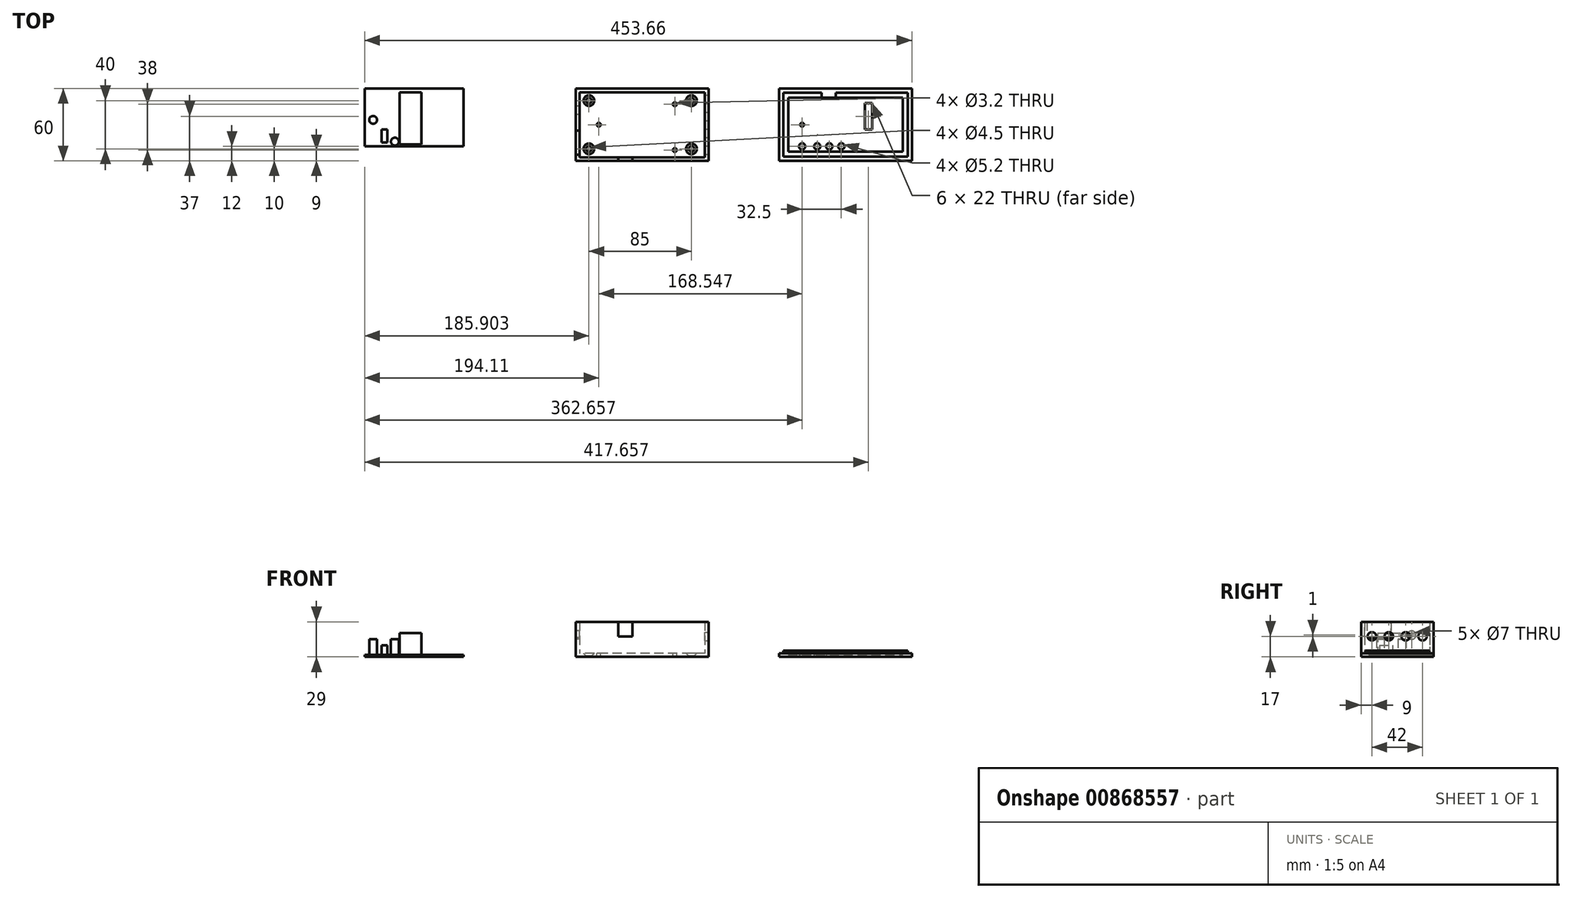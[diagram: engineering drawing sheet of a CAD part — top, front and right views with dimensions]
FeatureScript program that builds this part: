
annotation { "Feature Type Name" : "Feature", "Feature Type Description" : "" }
export const myFeature = defineFeature(function(context is Context, id is Id, definition is map)
    precondition{}
    {
        {
            var Q0;
            Q0=qCreatedBy(makeId("Top.planeOp"),FACE);
            var sketch = newSketch(context, id + "F0", { "sketchPlane" : qUnion([Q0])});
            skLineSegment(sketch, "E0.bottom", {"start": v(0, 0) * mm, "end": v(-110, 0) * mm});
            skLineSegment(sketch, "E0.top", {"start": v(0, -60) * mm, "end": v(-110, -60) * mm});
            skLineSegment(sketch, "E0.left", {"start": v(0, 0) * mm, "end": v(0, -60) * mm});
            skLineSegment(sketch, "E0.right", {"start": v(-110, 0) * mm, "end": v(-110, -60) * mm});
            skSolve(sketch);
        }
        {
            var Q0;
            Q0=makeQuery(id+"F0.imprint","IMPRINT",FACE,{"disambiguationData":[TD([[makeQuery(id+"F0.imprint","IMPRINT",EDGE,{"derivedFrom":sQuery(id+"F0.wireOp",EDGE,"E0.bottom")}),1.0]])]});
            extrude(context, id + "F1", {"entities" : qUnion([Q0]), "depth" : 3 * mm, "offsetDistance" : 25 * mm});
        }
        {
            var Q0;
            Q0=makeQuery(id+"F1.opExtrude","CAP_FACE",FACE,{"disambiguationData":[OSD([sQuery(id+"F0.wireOp",EDGE,"E0.bottom"),sQuery(id+"F0.wireOp",EDGE,"E0.top"),sQuery(id+"F0.wireOp",EDGE,"E0.left"),sQuery(id+"F0.wireOp",EDGE,"E0.right")])],"isStart":false});
            var sketch = newSketch(context, id + "F2", { "sketchPlane" : qUnion([Q0])});
            skLineSegment(sketch, "E1.0", {"start": v(-107, -3) * mm, "end": v(-107, -57) * mm});
            skLineSegment(sketch, "E1.1", {"start": v(-3, -3) * mm, "end": v(-107, -3) * mm});
            skLineSegment(sketch, "E1.2", {"start": v(-3, -3) * mm, "end": v(-3, -57) * mm});
            skLineSegment(sketch, "E1.3", {"start": v(-3, -57) * mm, "end": v(-107, -57) * mm});
            skPoint(sketch, "E2", {"position": v(-3, -30) * mm});
            skLineSegment(sketch, "E3", {"start": v(-3, -30) * mm, "end": v(-107, -30) * mm, "construction": true});
            skPoint(sketch, "E4", {"position": v(-52, -30) * mm});
            skLineSegment(sketch, "E5", {"start": v(-52, -30) * mm, "end": v(-52, -38.53) * mm, "construction": true});
            skPoint(sketch, "E6", {"position": v(-99.2, -50) * mm});
            skPoint(sketch, "E7.MirrorP", {"position": v(-99.2, -10) * mm});
            skLineSegment(sketch, "E8.MirrorCS", {"start": v(-52, -30) * mm, "end": v(-52, -21.47) * mm, "construction": true});
            skPoint(sketch, "E9", {"position": v(-14.2, -50) * mm});
            skPoint(sketch, "E10.MirrorP", {"position": v(-14.2, -10) * mm});
            skSolve(sketch);
        }
        {
            var Q0;
            Q0=makeQuery(id+"F2.imprint","IMPRINT",FACE,{"disambiguationData":[TD([[makeQuery(id+"F2.imprint","IMPRINT",EDGE,{"derivedFrom":sQuery(id+"F2.wireOp",EDGE,"E1.0")}),-1.0]])]});
            extrude(context, id + "F3", {"entities" : qUnion([Q0]), "operationType" : NewBodyOperationType.ADD, "depth" : 24 * mm, "offsetDistance" : 25 * mm});
        }
        {
            var Q0;
            {var subQ0=sQuery(id+"F0.wireOp",EDGE,"E0.right");Q0=makeQuery(id+"F3.boolean.opBoolean","MERGE",FACE,{"derivedFrom":[makeQuery(id+"F1.opExtrude","SWEPT_FACE",FACE,{"disambiguationData":[OSD([subQ0])]}),makeQuery(id+"F3.opExtrude","SWEPT_FACE",FACE,{"disambiguationData":[OSD([subQ0])]})]});}
            var sketch = newSketch(context, id + "F4", { "sketchPlane" : qUnion([Q0])});
            skPoint(sketch, "E11", {"position": v(45, 24) * mm});
            skPoint(sketch, "E12", {"position": v(18, 18) * mm});
            skCircle(sketch, "E13", {"center": v(18, 18) * mm, "radius": 3.5 * mm});
            skPoint(sketch, "E14", {"position": v(45, 16) * mm});
            skLineSegment(sketch, "E15", {"start": v(45, 16) * mm, "end": v(55, 16) * mm});
            skLineSegment(sketch, "E16", {"start": v(45, 16) * mm, "end": v(35, 16) * mm});
            skLineSegment(sketch, "E17", {"start": v(35, 16) * mm, "end": v(35, 27) * mm});
            skLineSegment(sketch, "E18", {"start": v(55, 16) * mm, "end": v(55, 27) * mm});
            skPoint(sketch, "E18.endSnap0", {"position": v(30, 27) * mm});
            skSolve(sketch);
        }
        {
            var Q0;
            Q0=makeQuery(id+"F4.imprint","IMPRINT",FACE,{"disambiguationData":[TD([[makeQuery(id+"F4.imprint","IMPRINT",EDGE,{"derivedFrom":sQuery(id+"F4.wireOp",EDGE,"a7Mlz7Xj-MbBD-aRSO-vmKB-jrrkiIna5h4T")}),1.0]])]});
            var Q1;
            Q1=makeQuery(id+"F4.imprint","IMPRINT",FACE,{"disambiguationData":[TD([[makeQuery(id+"F4.imprint","IMPRINT",EDGE,{"derivedFrom":sQuery(id+"F4.wireOp",EDGE,"E13")}),1.0]])]});
            var Q2;
            Q2=makeQuery(id+"F4.imprint","IMPRINT",FACE,{"disambiguationData":[TD([[makeQuery(id+"F4.imprint","IMPRINT",EDGE,{"derivedFrom":sQuery(id+"F4.wireOp",EDGE,"E15")}),1.0]])]});
            extrude(context, id + "F5", {"entities" : qUnion([Q0, Q1, Q2]), "operationType" : NewBodyOperationType.REMOVE, "oppositeDirection" : true, "depth" : 25 * mm, "offsetDistance" : 25 * mm});
        }
        {
            var Q0;
            Q0=makeQuery(id+"F2.imprint","IMPRINT",FACE,{"disambiguationData":[TD([[makeQuery(id+"F2.imprint","IMPRINT",EDGE,{"derivedFrom":sQuery(id+"F2.wireOp",EDGE,"E1.0")}),1.0]])]});
            var sketch = newSketch(context, id + "F6", { "sketchPlane" : qUnion([Q0])});
            skPoint(sketch, "E19.0", {"position": v(-107, -30) * mm});
            skPoint(sketch, "E20.0", {"position": v(-107, -3) * mm});
            skPoint(sketch, "E21.0", {"position": v(-107, -57) * mm});
            skPoint(sketch, "E22.0", {"position": v(-3, -3) * mm});
            skPoint(sketch, "E23.0", {"position": v(-3, -30) * mm});
            skPoint(sketch, "E24.0", {"position": v(-3, -57) * mm});
            skPoint(sketch, "E25", {"position": v(-91, -30) * mm});
            skCircle(sketch, "E26", {"center": v(-91, -30) * mm, "radius": 1.6 * mm});
            skPoint(sketch, "E27", {"position": v(-28, -30) * mm});
            skLineSegment(sketch, "E28", {"start": v(-28, -30) * mm, "end": v(-28, -51) * mm, "construction": true});
            skCircle(sketch, "E29", {"center": v(-28, -51) * mm, "radius": 1.6 * mm});
            skCircle(sketch, "E30", {"center": v(-28, -13) * mm, "radius": 1.6 * mm});
            skSolve(sketch);
        }
        {
            var Q0;
            Q0=makeQuery(id+"F6.imprint","IMPRINT",FACE,{"disambiguationData":[TD([[makeQuery(id+"F6.imprint","IMPRINT",EDGE,{"derivedFrom":sQuery(id+"F6.wireOp",EDGE,"E29")}),1.0]])]});
            var Q1;
            Q1=makeQuery(id+"F6.imprint","IMPRINT",FACE,{"disambiguationData":[TD([[makeQuery(id+"F6.imprint","IMPRINT",EDGE,{"derivedFrom":sQuery(id+"F6.wireOp",EDGE,"E30")}),1.0]])]});
            var Q2;
            Q2=makeQuery(id+"F6.imprint","IMPRINT",FACE,{"disambiguationData":[TD([[makeQuery(id+"F6.imprint","IMPRINT",EDGE,{"derivedFrom":sQuery(id+"F6.wireOp",EDGE,"E26")}),1.0]])]});
            extrude(context, id + "F7", {"entities" : qUnion([Q0, Q1, Q2]), "operationType" : NewBodyOperationType.REMOVE, "oppositeDirection" : true, "depth" : 25 * mm, "offsetDistance" : 25 * mm});
        }
        {
            var Q0;
            {var subQ0=sQuery(id+"F0.wireOp",EDGE,"E0.top");Q0=makeQuery(id+"F3.boolean.opBoolean","MERGE",FACE,{"derivedFrom":[makeQuery(id+"F1.opExtrude","SWEPT_FACE",FACE,{"disambiguationData":[OSD([subQ0])]}),makeQuery(id+"F3.opExtrude","SWEPT_FACE",FACE,{"disambiguationData":[OSD([subQ0])]})]});}
            var sketch = newSketch(context, id + "F8", { "sketchPlane" : qUnion([Q0])});
            skPoint(sketch, "E31", {"position": v(-75, 27) * mm});
            skPoint(sketch, "E32", {"position": v(-63, 27) * mm});
            skPoint(sketch, "E33", {"position": v(-75, 17) * mm});
            skLineSegment(sketch, "E34", {"start": v(-75, 17) * mm, "end": v(-75, 27) * mm});
            skLineSegment(sketch, "E35", {"start": v(-75, 17) * mm, "end": v(-63, 17) * mm});
            skLineSegment(sketch, "E36", {"start": v(-63, 17) * mm, "end": v(-63, 27) * mm});
            skSolve(sketch);
        }
        {
            var Q0;
            {var subQ0=sQuery(id+"F8.wireOp",EDGE,"E34");Q0=makeQuery(id+"F8.imprint","IMPRINT",FACE,{"disambiguationData":[TD([[makeQuery(id+"F8.imprint","IMPRINT",EDGE,{"derivedFrom":subQ0}),-1.0]])]});}
            extrude(context, id + "F9", {"entities" : qUnion([Q0]), "operationType" : NewBodyOperationType.REMOVE, "oppositeDirection" : true, "depth" : 25 * mm, "offsetDistance" : 25 * mm});
        }
        {
            var Q0;
            {var subQ0=sQuery(id+"F0.wireOp",EDGE,"E0.left");Q0=makeQuery(id+"F3.boolean.opBoolean","MERGE",FACE,{"derivedFrom":[makeQuery(id+"F1.opExtrude","SWEPT_FACE",FACE,{"disambiguationData":[OSD([subQ0])]}),makeQuery(id+"F3.opExtrude","SWEPT_FACE",FACE,{"disambiguationData":[OSD([subQ0])]})]});}
            var sketch = newSketch(context, id + "F10", { "sketchPlane" : qUnion([Q0])});
            skPoint(sketch, "E37", {"position": v(-60, 17) * mm});
            skLineSegment(sketch, "E38", {"start": v(-60, 17) * mm, "end": v(0, 17) * mm, "construction": true});
            skCircle(sketch, "E39", {"center": v(-51, 17) * mm, "radius": 3.5 * mm});
            skCircle(sketch, "E40.1.0.0", {"center": v(-37, 17) * mm, "radius": 3.5 * mm});
            skCircle(sketch, "E40.2.0.0", {"center": v(-23, 17) * mm, "radius": 3.5 * mm});
            skCircle(sketch, "E40.3.0.0", {"center": v(-9, 17) * mm, "radius": 3.5 * mm});
            skLineSegment(sketch, "E40.direction1", {"start": v(-51, 17) * mm, "end": v(-37, 17) * mm, "construction": true});
            skSolve(sketch);
        }
        {
            var Q0;
            Q0=makeQuery(id+"F10.imprint","IMPRINT",FACE,{"disambiguationData":[TD([[makeQuery(id+"F10.imprint","IMPRINT",EDGE,{"derivedFrom":sQuery(id+"F10.wireOp",EDGE,"E39")}),1.0]])]});
            var Q1;
            Q1=makeQuery(id+"F10.imprint","IMPRINT",FACE,{"disambiguationData":[TD([[makeQuery(id+"F10.imprint","IMPRINT",EDGE,{"derivedFrom":sQuery(id+"F10.wireOp",EDGE,"E40.1.0.0")}),1.0]])]});
            var Q2;
            Q2=makeQuery(id+"F10.imprint","IMPRINT",FACE,{"disambiguationData":[TD([[makeQuery(id+"F10.imprint","IMPRINT",EDGE,{"derivedFrom":sQuery(id+"F10.wireOp",EDGE,"E40.2.0.0")}),1.0]])]});
            var Q3;
            Q3=makeQuery(id+"F10.imprint","IMPRINT",FACE,{"disambiguationData":[TD([[makeQuery(id+"F10.imprint","IMPRINT",EDGE,{"derivedFrom":sQuery(id+"F10.wireOp",EDGE,"E40.3.0.0")}),1.0]])]});
            extrude(context, id + "F11", {"entities" : qUnion([Q0, Q1, Q2, Q3]), "operationType" : NewBodyOperationType.REMOVE, "oppositeDirection" : true, "depth" : 25 * mm, "offsetDistance" : 25 * mm});
        }
        {
            var Q0;
            {var subQ0=sQuery(id+"F0.wireOp",EDGE,"E0.top");var subQ1=sQuery(id+"F0.wireOp",EDGE,"E0.bottom");var subQ2=sQuery(id+"F2.wireOp",EDGE,"E1.3");var subQ3=sQuery(id+"F2.wireOp",EDGE,"E1.0");var subQ4=sQuery(id+"F0.wireOp",EDGE,"E0.left");var subQ5=sQuery(id+"F2.wireOp",EDGE,"E1.2");var subQ6=sQuery(id+"F0.wireOp",EDGE,"E0.right");var subQ7=sQuery(id+"F2.wireOp",EDGE,"E1.1");Q0=makeQuery(id+"F9.boolean.opBoolean","SPLIT",FACE,{"disambiguationData":[TD([makeQuery(id+"F1.opExtrude","SWEPT_FACE",FACE,{"disambiguationData":[OSD([subQ1])]})])],"derivedFrom":makeQuery(id+"F3.opExtrude","CAP_FACE",FACE,{"disambiguationData":[OSD([subQ1,subQ0,subQ4,subQ6,subQ3,subQ7,subQ5,subQ2])],"isStart":false})});}
            var Q1;
            {var subQ0=sQuery(id+"F0.wireOp",EDGE,"E0.right");var subQ1=sQuery(id+"F2.wireOp",EDGE,"E1.3");var subQ2=sQuery(id+"F2.wireOp",EDGE,"E1.0");var subQ3=sQuery(id+"F0.wireOp",EDGE,"E0.top");Q1=makeQuery(id+"F9.boolean.opBoolean","SPLIT",FACE,{"disambiguationData":[TD([makeQuery(id+"F5.boolean.opBoolean","COPY",FACE,{"derivedFrom":makeQuery(id+"F5.opExtrude","SWEPT_FACE",FACE,{"disambiguationData":[OSD([sQuery(id+"F4.wireOp",EDGE,"E18")])]})})])],"derivedFrom":makeQuery(id+"F3.opExtrude","CAP_FACE",FACE,{"disambiguationData":[OSD([sQuery(id+"F0.wireOp",EDGE,"E0.bottom"),subQ3,sQuery(id+"F0.wireOp",EDGE,"E0.left"),subQ0,subQ2,sQuery(id+"F2.wireOp",EDGE,"E1.1"),sQuery(id+"F2.wireOp",EDGE,"E1.2"),subQ1])],"isStart":false})});}
            extrude(context, id + "F12", {"entities" : qUnion([Q0, Q1]), "operationType" : NewBodyOperationType.ADD, "depth" : 2 * mm, "offsetDistance" : 25 * mm});
        }
        {
            var Q0;
            Q0=sQuery(id+"F2.wireOp",VERTEX,"E7.MirrorP");
            var Q1;
            Q1=sQuery(id+"F2.wireOp",VERTEX,"E6");
            var Q2;
            Q2=sQuery(id+"F2.wireOp",VERTEX,"E9");
            var Q3;
            Q3=sQuery(id+"F2.wireOp",VERTEX,"E10.MirrorP");
            var Q4;
            Q4=makeQuery(id+"F1.opExtrude","SWEPT_BODY",BODY,{"disambiguationData":[OSD([sQuery(id+"F0.wireOp",EDGE,"E0.bottom"),sQuery(id+"F0.wireOp",EDGE,"E0.top"),sQuery(id+"F0.wireOp",EDGE,"E0.left"),sQuery(id+"F0.wireOp",EDGE,"E0.right")])]});
            hole(context, id + "F13", {"style" : HoleStyle.C_SINK, "endStyle" : HoleEndStyle.THROUGH, "standardTappedOrClearance" : lookupTablePath({ "fit" : "Normal", "standard" : "ISO", "size" : "M4", "type" : "Clearance" }), "standardBlindInLast" : lookupTablePath({ "fit" : "Normal", "standard" : "ISO", "size" : "M4", "type" : "Clearance" }), "holeDiameter" : 4.5 * mm, "cSinkDiameter" : 8.96 * mm, "cSinkAngle" : 90 * degree, "majorDiameter" : 4 * mm, "isTappedThrough" : true, "tappedDepth" : 12 * mm, "tapClearance" : 3, "locations" : qUnion([Q0, Q1, Q2, Q3]), "scope" : qUnion([Q4])});
        }
        {
            var Q0;
            Q0=qCreatedBy(makeId("Top.planeOp"),FACE);
            var sketch = newSketch(context, id + "F14", { "sketchPlane" : qUnion([Q0])});
            skLineSegment(sketch, "E41.bottom", {"start": v(58.55, 0) * mm, "end": v(168.55, 0) * mm});
            skLineSegment(sketch, "E41.top", {"start": v(58.55, -60) * mm, "end": v(168.55, -60) * mm});
            skLineSegment(sketch, "E41.left", {"start": v(58.55, 0) * mm, "end": v(58.55, -60) * mm});
            skLineSegment(sketch, "E41.right", {"start": v(168.55, 0) * mm, "end": v(168.55, -60) * mm});
            skSolve(sketch);
        }
        {
            var Q0;
            Q0=makeQuery(id+"F14.imprint","IMPRINT",FACE,{"disambiguationData":[TD([[makeQuery(id+"F14.imprint","IMPRINT",EDGE,{"derivedFrom":sQuery(id+"F14.wireOp",EDGE,"E41.bottom")}),-1.0]])]});
            extrude(context, id + "F15", {"entities" : qUnion([Q0]), "depth" : 3 * mm, "offsetDistance" : 25 * mm});
        }
        {
            var Q0;
            Q0=makeQuery(id+"F15.opExtrude","CAP_FACE",FACE,{"disambiguationData":[OSD([sQuery(id+"F14.wireOp",EDGE,"E41.bottom"),sQuery(id+"F14.wireOp",EDGE,"E41.top"),sQuery(id+"F14.wireOp",EDGE,"E41.left"),sQuery(id+"F14.wireOp",EDGE,"E41.right")])],"isStart":false});
            var sketch = newSketch(context, id + "F16", { "sketchPlane" : qUnion([Q0])});
            skLineSegment(sketch, "E42.0", {"start": v(62.05, -56.5) * mm, "end": v(165.05, -56.5) * mm});
            skLineSegment(sketch, "E42.1", {"start": v(62.05, -3.5) * mm, "end": v(62.05, -56.5) * mm});
            skLineSegment(sketch, "E42.2", {"start": v(62.05, -3.5) * mm, "end": v(165.05, -3.5) * mm});
            skLineSegment(sketch, "E42.3", {"start": v(165.05, -3.5) * mm, "end": v(165.05, -56.5) * mm});
            skPoint(sketch, "E43", {"position": v(77.55, -30) * mm});
            skPoint(sketch, "E43.positionSnap0", {"position": v(58.55, -30) * mm});
            skCircle(sketch, "E44", {"center": v(77.55, -30) * mm, "radius": 1.6 * mm});
            skSolve(sketch);
        }
        {
            var Q0;
            Q0=makeQuery(id+"F16.imprint","IMPRINT",FACE,{"disambiguationData":[TD([[makeQuery(id+"F16.imprint","IMPRINT",EDGE,{"derivedFrom":sQuery(id+"F16.wireOp",EDGE,"E44")}),1.0]])]});
            extrude(context, id + "F17", {"entities" : qUnion([Q0]), "operationType" : NewBodyOperationType.REMOVE, "oppositeDirection" : true, "depth" : 25 * mm, "offsetDistance" : 25 * mm});
        }
        {
            var Q0;
            Q0 = qSketchRegion(id + "F16", true);
            extrude(context, id + "F18", {"entities" : qUnion([Q0]), "operationType" : NewBodyOperationType.ADD, "depth" : 2 * mm, "offsetDistance" : 25 * mm});
        }
        {
            var Q0;
            Q0=makeQuery(id+"F18.opExtrude","CAP_FACE",FACE,{"disambiguationData":[OSD([sQuery(id+"F16.wireOp",EDGE,"E42.0"),sQuery(id+"F16.wireOp",EDGE,"E42.1"),sQuery(id+"F16.wireOp",EDGE,"E42.2"),sQuery(id+"F16.wireOp",EDGE,"E42.3"),sQuery(id+"F16.wireOp",EDGE,"E44")])],"isStart":false});
            var sketch = newSketch(context, id + "F19", { "sketchPlane" : qUnion([Q0])});
            skLineSegment(sketch, "E45", {"start": v(165.05, -56.5) * mm, "end": v(62.05, -3.5) * mm, "construction": true});
            skLineSegment(sketch, "E46.bottom", {"start": v(66.05, -52.5) * mm, "end": v(161.05, -52.5) * mm});
            skLineSegment(sketch, "E46.top", {"start": v(66.05, -7.5) * mm, "end": v(161.05, -7.5) * mm});
            skLineSegment(sketch, "E46.left", {"start": v(66.05, -52.5) * mm, "end": v(66.05, -7.5) * mm});
            skLineSegment(sketch, "E46.right", {"start": v(161.05, -52.5) * mm, "end": v(161.05, -7.5) * mm});
            skPoint(sketch, "E46.middle", {"position": v(113.55, -30) * mm});
            skSolve(sketch);
        }
        {
            var Q0;
            Q0=makeQuery(id+"F19.imprint","IMPRINT",FACE,{"disambiguationData":[TD([[makeQuery(id+"F19.imprint","IMPRINT",EDGE,{"derivedFrom":sQuery(id+"F19.wireOp",EDGE,"E46.bottom")}),1.0]])]});
            extrude(context, id + "F20", {"entities" : qUnion([Q0]), "operationType" : NewBodyOperationType.REMOVE, "oppositeDirection" : true, "depth" : 3 * mm, "offsetDistance" : 25 * mm});
        }
        {
            var Q0;
            Q0=makeQuery(id+"F18.opExtrude","CAP_FACE",FACE,{"disambiguationData":[OSD([sQuery(id+"F16.wireOp",EDGE,"E42.0"),sQuery(id+"F16.wireOp",EDGE,"E42.1"),sQuery(id+"F16.wireOp",EDGE,"E42.2"),sQuery(id+"F16.wireOp",EDGE,"E42.3"),sQuery(id+"F16.wireOp",EDGE,"E44")])],"isStart":false});
            var sketch = newSketch(context, id + "F21", { "sketchPlane" : qUnion([Q0])});
            skPoint(sketch, "E47.0", {"position": v(58.55, 0) * mm});
            skPoint(sketch, "E48", {"position": v(93.55, -3.5) * mm});
            skLineSegment(sketch, "E49", {"start": v(93.55, -3.5) * mm, "end": v(93.55, -7.5) * mm});
            skLineSegment(sketch, "E50", {"start": v(105.55, -3.5) * mm, "end": v(105.55, -7.5) * mm});
            skSolve(sketch);
        }
        {
            var Q0;
            {var subQ0=sQuery(id+"F21.wireOp",EDGE,"E49");Q0=makeQuery(id+"F21.imprint","IMPRINT",FACE,{"disambiguationData":[TD([[makeQuery(id+"F21.imprint","IMPRINT",EDGE,{"derivedFrom":subQ0}),1.0]])]});}
            extrude(context, id + "F22", {"entities" : qUnion([Q0]), "operationType" : NewBodyOperationType.REMOVE, "oppositeDirection" : true, "depth" : 2 * mm, "offsetDistance" : 25 * mm});
        }
        {
            var Q0;
            Q0=makeQuery(id+"F15.opExtrude","CAP_FACE",FACE,{"disambiguationData":[OSD([sQuery(id+"F14.wireOp",EDGE,"E41.bottom"),sQuery(id+"F14.wireOp",EDGE,"E41.top"),sQuery(id+"F14.wireOp",EDGE,"E41.left"),sQuery(id+"F14.wireOp",EDGE,"E41.right")])],"isStart":true});
            var sketch = newSketch(context, id + "F23", { "sketchPlane" : qUnion([Q0])});
            skLineSegment(sketch, "E51", {"start": v(58.55, 48) * mm, "end": v(168.55, 48) * mm, "construction": true});
            skCircle(sketch, "E52", {"center": v(77.55, 48) * mm, "radius": 2.6 * mm});
            skCircle(sketch, "E53", {"center": v(90.05, 48) * mm, "radius": 2.6 * mm});
            skCircle(sketch, "E54", {"center": v(100.05, 48) * mm, "radius": 2.6 * mm});
            skCircle(sketch, "E55", {"center": v(110.05, 48) * mm, "radius": 2.6 * mm});
            skPoint(sketch, "E56", {"position": v(129.55, 0) * mm});
            skPoint(sketch, "E57", {"position": v(129.55, 12) * mm});
            skPoint(sketch, "E58", {"position": v(129.55, 34) * mm});
            skLineSegment(sketch, "E59", {"start": v(129.55, 12) * mm, "end": v(129.55, 34) * mm});
            skLineSegment(sketch, "E60", {"start": v(129.55, 34) * mm, "end": v(135.55, 34) * mm});
            skLineSegment(sketch, "E61", {"start": v(135.55, 34) * mm, "end": v(135.55, 12) * mm});
            skLineSegment(sketch, "E62", {"start": v(135.55, 12) * mm, "end": v(129.55, 12) * mm});
            skSolve(sketch);
        }
        {
            var Q0;
            Q0=makeQuery(id+"F23.imprint","IMPRINT",FACE,{"disambiguationData":[TD([[makeQuery(id+"F23.imprint","IMPRINT",EDGE,{"derivedFrom":sQuery(id+"F23.wireOp",EDGE,"E55")}),1.0]])]});
            var Q1;
            Q1=makeQuery(id+"F23.imprint","IMPRINT",FACE,{"disambiguationData":[TD([[makeQuery(id+"F23.imprint","IMPRINT",EDGE,{"derivedFrom":sQuery(id+"F23.wireOp",EDGE,"E54")}),1.0]])]});
            var Q2;
            Q2=makeQuery(id+"F23.imprint","IMPRINT",FACE,{"disambiguationData":[TD([[makeQuery(id+"F23.imprint","IMPRINT",EDGE,{"derivedFrom":sQuery(id+"F23.wireOp",EDGE,"E53")}),1.0]])]});
            var Q3;
            Q3=makeQuery(id+"F23.imprint","IMPRINT",FACE,{"disambiguationData":[TD([[makeQuery(id+"F23.imprint","IMPRINT",EDGE,{"derivedFrom":sQuery(id+"F23.wireOp",EDGE,"E52")}),1.0]])]});
            var Q4;
            Q4=makeQuery(id+"F23.imprint","IMPRINT",FACE,{"disambiguationData":[TD([[makeQuery(id+"F23.imprint","IMPRINT",EDGE,{"derivedFrom":sQuery(id+"F23.wireOp",EDGE,"E59")}),-1.0]])]});
            extrude(context, id + "F24", {"entities" : qUnion([Q0, Q1, Q2, Q3, Q4]), "operationType" : NewBodyOperationType.REMOVE, "oppositeDirection" : true, "depth" : 25 * mm, "offsetDistance" : 25 * mm});
        }
        {
            var Q0;
            Q0=qCreatedBy(makeId("Top.planeOp"),FACE);
            var sketch = newSketch(context, id + "F25", { "sketchPlane" : qUnion([Q0])});
            skLineSegment(sketch, "E63.bottom", {"start": v(-203.11, 0) * mm, "end": v(-285.11, 0) * mm});
            skLineSegment(sketch, "E63.top", {"start": v(-203.11, -48) * mm, "end": v(-285.11, -48) * mm});
            skLineSegment(sketch, "E63.left", {"start": v(-203.11, 0) * mm, "end": v(-203.11, -48) * mm});
            skLineSegment(sketch, "E63.right", {"start": v(-285.11, 0) * mm, "end": v(-285.11, -48) * mm});
            skSolve(sketch);
        }
        {
            var Q0;
            Q0 = qSketchRegion(id + "F25", true);
            var Q1;
            Q1=makeQuery(id+"F25.imprint","IMPRINT",FACE,{"disambiguationData":[TD([[makeQuery(id+"F25.imprint","IMPRINT",EDGE,{"derivedFrom":sQuery(id+"F25.wireOp",EDGE,"E63.bottom")}),1.0]])]});
            extrude(context, id + "F26", {"entities" : qUnion([Q0, Q1]), "depth" : 1.7 * mm, "offsetDistance" : 25 * mm});
        }
        {
            var Q0;
            Q0=makeQuery(id+"F26.opExtrude","CAP_FACE",FACE,{"disambiguationData":[OSD([sQuery(id+"F25.wireOp",EDGE,"E63.bottom"),sQuery(id+"F25.wireOp",EDGE,"E63.top"),sQuery(id+"F25.wireOp",EDGE,"E63.left"),sQuery(id+"F25.wireOp",EDGE,"E63.right")])],"isStart":false});
            var sketch = newSketch(context, id + "F27", { "sketchPlane" : qUnion([Q0])});
            skPoint(sketch, "E64", {"position": v(-271.11, -44.8) * mm});
            skLineSegment(sketch, "E65.bottom", {"start": v(-271.11, -44.8) * mm, "end": v(-266.31, -44.8) * mm});
            skLineSegment(sketch, "E65.top", {"start": v(-271.11, -33.8) * mm, "end": v(-266.31, -33.8) * mm});
            skLineSegment(sketch, "E65.left", {"start": v(-271.11, -44.8) * mm, "end": v(-271.11, -33.8) * mm});
            skLineSegment(sketch, "E65.right", {"start": v(-266.31, -44.8) * mm, "end": v(-266.31, -33.8) * mm});
            skPoint(sketch, "E66", {"position": v(-278.11, -26) * mm});
            skCircle(sketch, "E67", {"center": v(-278.11, -26) * mm, "radius": 3.25 * mm});
            skPoint(sketch, "E68", {"position": v(-260.11, -44) * mm});
            skCircle(sketch, "E69", {"center": v(-260.11, -44) * mm, "radius": 3.25 * mm});
            skPoint(sketch, "E70", {"position": v(-256.11, -46.2) * mm});
            skLineSegment(sketch, "E71.bottom", {"start": v(-256.11, -46.2) * mm, "end": v(-238.11, -46.2) * mm});
            skLineSegment(sketch, "E71.top", {"start": v(-256.11, -3.2) * mm, "end": v(-238.11, -3.2) * mm});
            skLineSegment(sketch, "E71.left", {"start": v(-256.11, -46.2) * mm, "end": v(-256.11, -3.2) * mm});
            skLineSegment(sketch, "E71.right", {"start": v(-238.11, -46.2) * mm, "end": v(-238.11, -3.2) * mm});
            skSolve(sketch);
        }
        {
            var Q0;
            Q0=makeQuery(id+"F27.imprint","IMPRINT",FACE,{"disambiguationData":[TD([[makeQuery(id+"F27.imprint","IMPRINT",EDGE,{"derivedFrom":sQuery(id+"F27.wireOp",EDGE,"E69")}),1.0]])]});
            var Q1;
            Q1=makeQuery(id+"F27.imprint","IMPRINT",FACE,{"disambiguationData":[TD([[makeQuery(id+"F27.imprint","IMPRINT",EDGE,{"derivedFrom":sQuery(id+"F27.wireOp",EDGE,"E67")}),1.0]])]});
            extrude(context, id + "F28", {"entities" : qUnion([Q0, Q1]), "operationType" : NewBodyOperationType.ADD, "depth" : 13 * mm, "offsetDistance" : 25 * mm});
        }
        {
            var Q0;
            Q0=makeQuery(id+"F27.imprint","IMPRINT",FACE,{"disambiguationData":[TD([[makeQuery(id+"F27.imprint","IMPRINT",EDGE,{"derivedFrom":sQuery(id+"F27.wireOp",EDGE,"E65.bottom")}),1.0]])]});
            extrude(context, id + "F29", {"entities" : qUnion([Q0]), "operationType" : NewBodyOperationType.ADD, "depth" : 8 * mm, "offsetDistance" : 25 * mm});
        }
        {
            var Q0;
            Q0=makeQuery(id+"F27.imprint","IMPRINT",FACE,{"disambiguationData":[TD([[makeQuery(id+"F27.imprint","IMPRINT",EDGE,{"derivedFrom":sQuery(id+"F27.wireOp",EDGE,"E71.bottom")}),1.0]])]});
            extrude(context, id + "F30", {"entities" : qUnion([Q0]), "operationType" : NewBodyOperationType.ADD, "depth" : 18 * mm, "offsetDistance" : 25 * mm});
        }
    });
